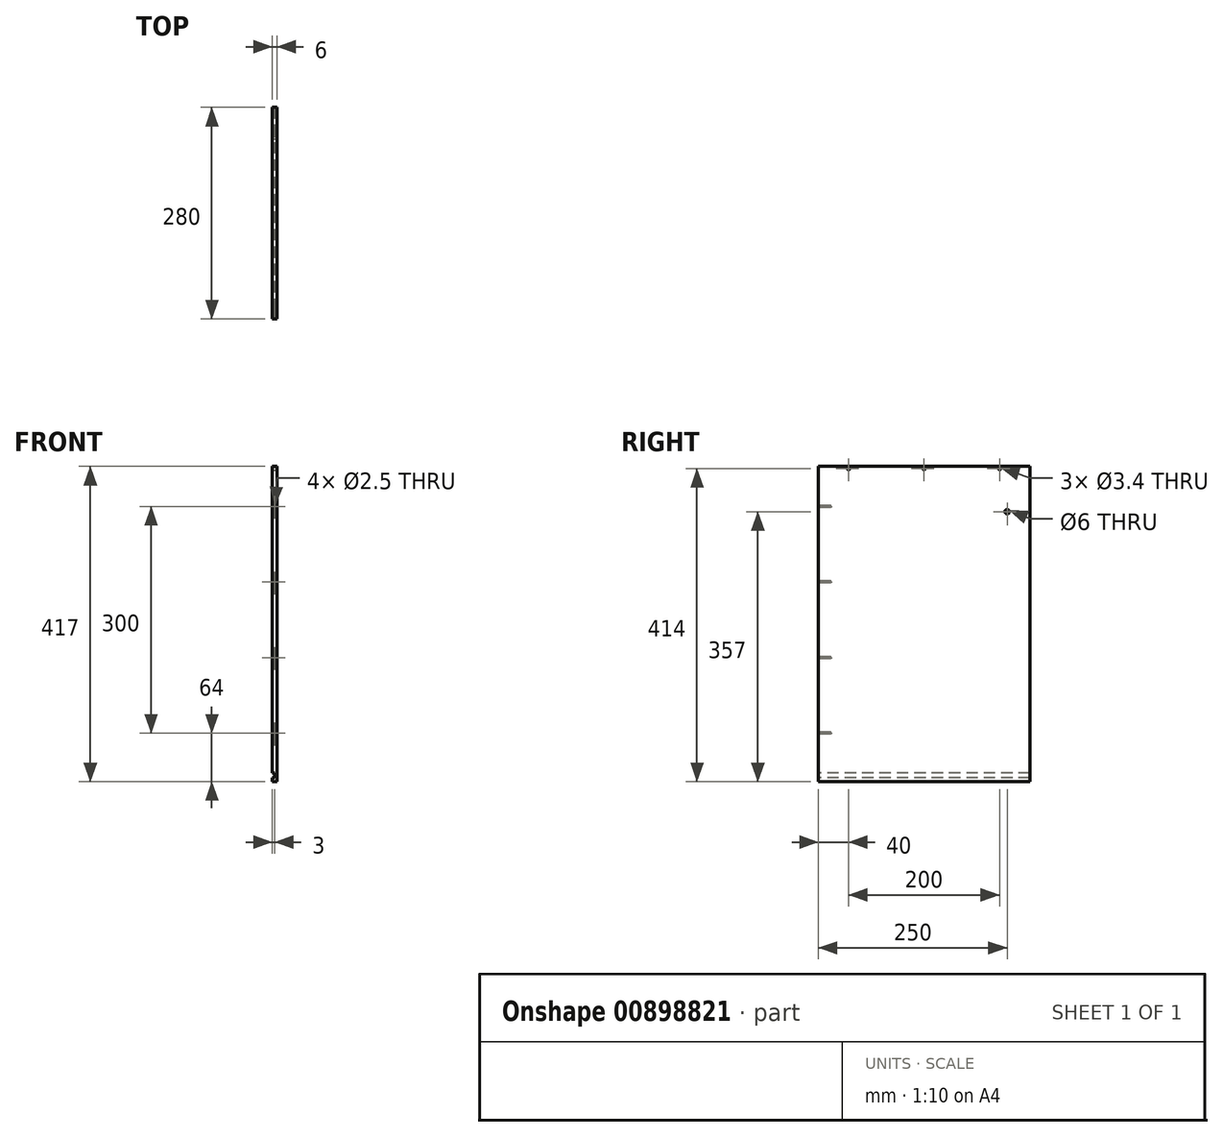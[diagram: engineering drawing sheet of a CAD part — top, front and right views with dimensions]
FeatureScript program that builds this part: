
annotation { "Feature Type Name" : "Feature", "Feature Type Description" : "" }
export const myFeature = defineFeature(function(context is Context, id is Id, definition is map)
    precondition{}
    {
        {
            var Q0;
            Q0=qCreatedBy(makeId("Right.planeOp"),FACE);
            var sketch = newSketch(context, id + "F0", { "sketchPlane" : qUnion([Q0])});
            skLineSegment(sketch, "E0.bottom", {"start": v(140, 208.5) * mm, "end": v(-140, 208.5) * mm});
            skLineSegment(sketch, "E0.top", {"start": v(140, -208.5) * mm, "end": v(-140, -208.5) * mm});
            skLineSegment(sketch, "E0.left", {"start": v(140, 208.5) * mm, "end": v(140, -208.5) * mm});
            skLineSegment(sketch, "E0.right", {"start": v(-140, 208.5) * mm, "end": v(-140, -208.5) * mm});
            skPoint(sketch, "E0.middle", {"position": v(0, 0) * mm});
            skSolve(sketch);
        }
        {
            var Q0;
            Q0=makeQuery(id+"F0.imprint","IMPRINT",FACE,{"disambiguationData":[TD([[makeQuery(id+"F0.imprint","IMPRINT",EDGE,{"derivedFrom":sQuery(id+"F0.wireOp",EDGE,"E0.bottom")}),1.0]])]});
            extrude(context, id + "F1", {"entities" : qUnion([Q0]), "depth" : 6 * mm, "offsetDistance" : 25 * mm});
        }
        {
            var Q0;
            Q0=makeQuery(id+"F1.opExtrude","CAP_FACE",FACE,{"disambiguationData":[OSD([sQuery(id+"F0.wireOp",EDGE,"E0.bottom"),sQuery(id+"F0.wireOp",EDGE,"E0.top"),sQuery(id+"F0.wireOp",EDGE,"E0.left"),sQuery(id+"F0.wireOp",EDGE,"E0.right")])],"isStart":false});
            var sketch = newSketch(context, id + "F2", { "sketchPlane" : qUnion([Q0])});
            skPoint(sketch, "E1", {"position": v(-100, 205.5) * mm});
            skPoint(sketch, "E2", {"position": v(0, 205.5) * mm});
            skPoint(sketch, "E3", {"position": v(100, 205.5) * mm});
            skPoint(sketch, "E4", {"position": v(110, 148.5) * mm});
            skSolve(sketch);
        }
        {
            var Q0;
            Q0=sQuery(id+"F2.wireOp",VERTEX,"E3");
            var Q1;
            Q1=sQuery(id+"F2.wireOp",VERTEX,"E2");
            var Q2;
            Q2=sQuery(id+"F2.wireOp",VERTEX,"E1");
            var Q3;
            Q3=makeQuery(id+"F1.opExtrude","SWEPT_BODY",BODY,{"disambiguationData":[OSD([sQuery(id+"F0.wireOp",EDGE,"E0.bottom"),sQuery(id+"F0.wireOp",EDGE,"E0.top"),sQuery(id+"F0.wireOp",EDGE,"E0.left"),sQuery(id+"F0.wireOp",EDGE,"E0.right")])]});
            hole(context, id + "F3", {"style" : HoleStyle.SIMPLE, "endStyle" : HoleEndStyle.THROUGH, "standardTappedOrClearance" : lookupTablePath({ "fit" : "Normal", "standard" : "ISO", "size" : "M3", "type" : "Clearance" }), "standardBlindInLast" : lookupTablePath({ "fit" : "Normal", "standard" : "ISO", "size" : "M3", "type" : "Clearance" }), "holeDiameter" : 3.4 * mm, "majorDiameter" : 3 * mm, "tappedDepth" : 15 * mm, "tapClearance" : 3, "locations" : qUnion([Q0, Q1, Q2]), "scope" : qUnion([Q3])});
        }
        {
            var Q0;
            Q0=makeQuery(id+"F1.opExtrude","CAP_FACE",FACE,{"disambiguationData":[OSD([sQuery(id+"F0.wireOp",EDGE,"E0.bottom"),sQuery(id+"F0.wireOp",EDGE,"E0.top"),sQuery(id+"F0.wireOp",EDGE,"E0.left"),sQuery(id+"F0.wireOp",EDGE,"E0.right")])],"isStart":true});
            var sketch = newSketch(context, id + "F4", { "sketchPlane" : qUnion([Q0])});
            skLineSegment(sketch, "E5.bottom", {"start": v(-140, -203.5) * mm, "end": v(140, -203.5) * mm});
            skLineSegment(sketch, "E5.top", {"start": v(-140, -197.4) * mm, "end": v(140, -197.4) * mm});
            skLineSegment(sketch, "E5.left", {"start": v(-140, -203.5) * mm, "end": v(-140, -197.4) * mm});
            skLineSegment(sketch, "E5.right", {"start": v(140, -203.5) * mm, "end": v(140, -197.4) * mm});
            skSolve(sketch);
        }
        {
            var Q0;
            Q0 = qSketchRegion(id + "F4", true);
            extrude(context, id + "F5", {"entities" : qUnion([Q0]), "oppositeDirection" : true, "depth" : 3 * mm, "offsetDistance" : 25 * mm});
        }
        {
            var Q0;
            Q0=makeQuery(id+"F5.opExtrude","SWEPT_BODY",BODY,{"disambiguationData":[OSD([sQuery(id+"F4.wireOp",EDGE,"E5.bottom"),sQuery(id+"F4.wireOp",EDGE,"E5.top"),sQuery(id+"F4.wireOp",EDGE,"E5.left"),sQuery(id+"F4.wireOp",EDGE,"E5.right")])]});
            var Q1;
            Q1=makeQuery(id+"F1.opExtrude","SWEPT_BODY",BODY,{"disambiguationData":[OSD([sQuery(id+"F0.wireOp",EDGE,"E0.bottom"),sQuery(id+"F0.wireOp",EDGE,"E0.top"),sQuery(id+"F0.wireOp",EDGE,"E0.left"),sQuery(id+"F0.wireOp",EDGE,"E0.right")])]});
            booleanBodies(context, id + "F6", {"operationType" : BooleanOperationType.SUBTRACTION, "tools" : qUnion([Q0]), "targets" : qUnion([Q1])});
        }
        {
            var Q0;
            Q0=makeQuery(id+"F1.opExtrude","SWEPT_FACE",FACE,{"disambiguationData":[OSD([sQuery(id+"F0.wireOp",EDGE,"E0.right")])]});
            var sketch = newSketch(context, id + "F7", { "sketchPlane" : qUnion([Q0])});
            skPoint(sketch, "E6", {"position": v(3, 155.5) * mm});
            skPoint(sketch, "E7", {"position": v(3, 55.5) * mm});
            skPoint(sketch, "E8", {"position": v(3, -44.5) * mm});
            skPoint(sketch, "E9", {"position": v(3, -144.5) * mm});
            skSolve(sketch);
        }
        {
            var Q0;
            Q0=sQuery(id+"F7.wireOp",VERTEX,"E6");
            var Q1;
            Q1=sQuery(id+"F7.wireOp",VERTEX,"E7");
            var Q2;
            Q2=sQuery(id+"F7.wireOp",VERTEX,"E8");
            var Q3;
            Q3=sQuery(id+"F7.wireOp",VERTEX,"119dda67-e599-40bb-9ecc-9a61b273a647");
            var Q4;
            Q4=makeQuery(id+"F1.opExtrude","SWEPT_BODY",BODY,{"disambiguationData":[OSD([sQuery(id+"F0.wireOp",EDGE,"E0.bottom"),sQuery(id+"F0.wireOp",EDGE,"E0.top"),sQuery(id+"F0.wireOp",EDGE,"E0.left"),sQuery(id+"F0.wireOp",EDGE,"E0.right")])]});
            hole(context, id + "F8", {"style" : HoleStyle.SIMPLE, "endStyle" : HoleEndStyle.BLIND, "standardTappedOrClearance" : lookupTablePath({ "standard" : "ISO", "engagement" : "75%", "pitch" : "0.5 mm", "size" : "M3", "type" : "Tapped" }), "standardBlindInLast" : lookupTablePath({ "standard" : "ISO", "engagement" : "75%", "pitch" : "0.5 mm", "size" : "M3", "type" : "Tapped" }), "holeDiameter" : 2.5 * mm, "majorDiameter" : 3 * mm, "showTappedDepth" : true, "holeDepth" : 16.5 * mm, "tappedDepth" : 15 * mm, "tapClearance" : 3, "locations" : qUnion([Q0, Q1, Q2, Q3]), "scope" : qUnion([Q4])});
        }
        {
            var Q0;
            Q0=sQuery(id+"F2.wireOp",VERTEX,"E4");
            var Q1;
            Q1=makeQuery(id+"F1.opExtrude","SWEPT_BODY",BODY,{"disambiguationData":[OSD([sQuery(id+"F0.wireOp",EDGE,"E0.bottom"),sQuery(id+"F0.wireOp",EDGE,"E0.top"),sQuery(id+"F0.wireOp",EDGE,"E0.left"),sQuery(id+"F0.wireOp",EDGE,"E0.right")])]});
            hole(context, id + "F9", {"style" : HoleStyle.SIMPLE, "endStyle" : HoleEndStyle.THROUGH, "holeDiameter" : 6 * mm, "majorDiameter" : 5 * mm, "tappedDepth" : 15 * mm, "tapClearance" : 3, "locations" : qUnion([Q0]), "scope" : qUnion([Q1])});
        }
        {
            var Q0;
            Q0=sQuery(id+"F7.wireOp",VERTEX,"E9");
            var Q1;
            Q1=makeQuery(id+"F1.opExtrude","SWEPT_BODY",BODY,{"disambiguationData":[OSD([sQuery(id+"F0.wireOp",EDGE,"E0.bottom"),sQuery(id+"F0.wireOp",EDGE,"E0.top"),sQuery(id+"F0.wireOp",EDGE,"E0.left"),sQuery(id+"F0.wireOp",EDGE,"E0.right")])]});
            hole(context, id + "F10", {"style" : HoleStyle.SIMPLE, "endStyle" : HoleEndStyle.BLIND, "standardTappedOrClearance" : lookupTablePath({ "standard" : "ISO", "engagement" : "75%", "pitch" : "0.5 mm", "size" : "M3", "type" : "Tapped" }), "standardBlindInLast" : lookupTablePath({ "standard" : "ISO", "fit" : "Normal", "engagement" : "75%", "pitch" : "0.5 mm", "size" : "M3", "type" : "Clearance & tapped" }), "holeDiameter" : 2.5 * mm, "majorDiameter" : 3 * mm, "showTappedDepth" : true, "holeDepth" : 16.5 * mm, "tappedDepth" : 15 * mm, "tapClearance" : 3, "locations" : qUnion([Q0]), "scope" : qUnion([Q1])});
        }
    });
